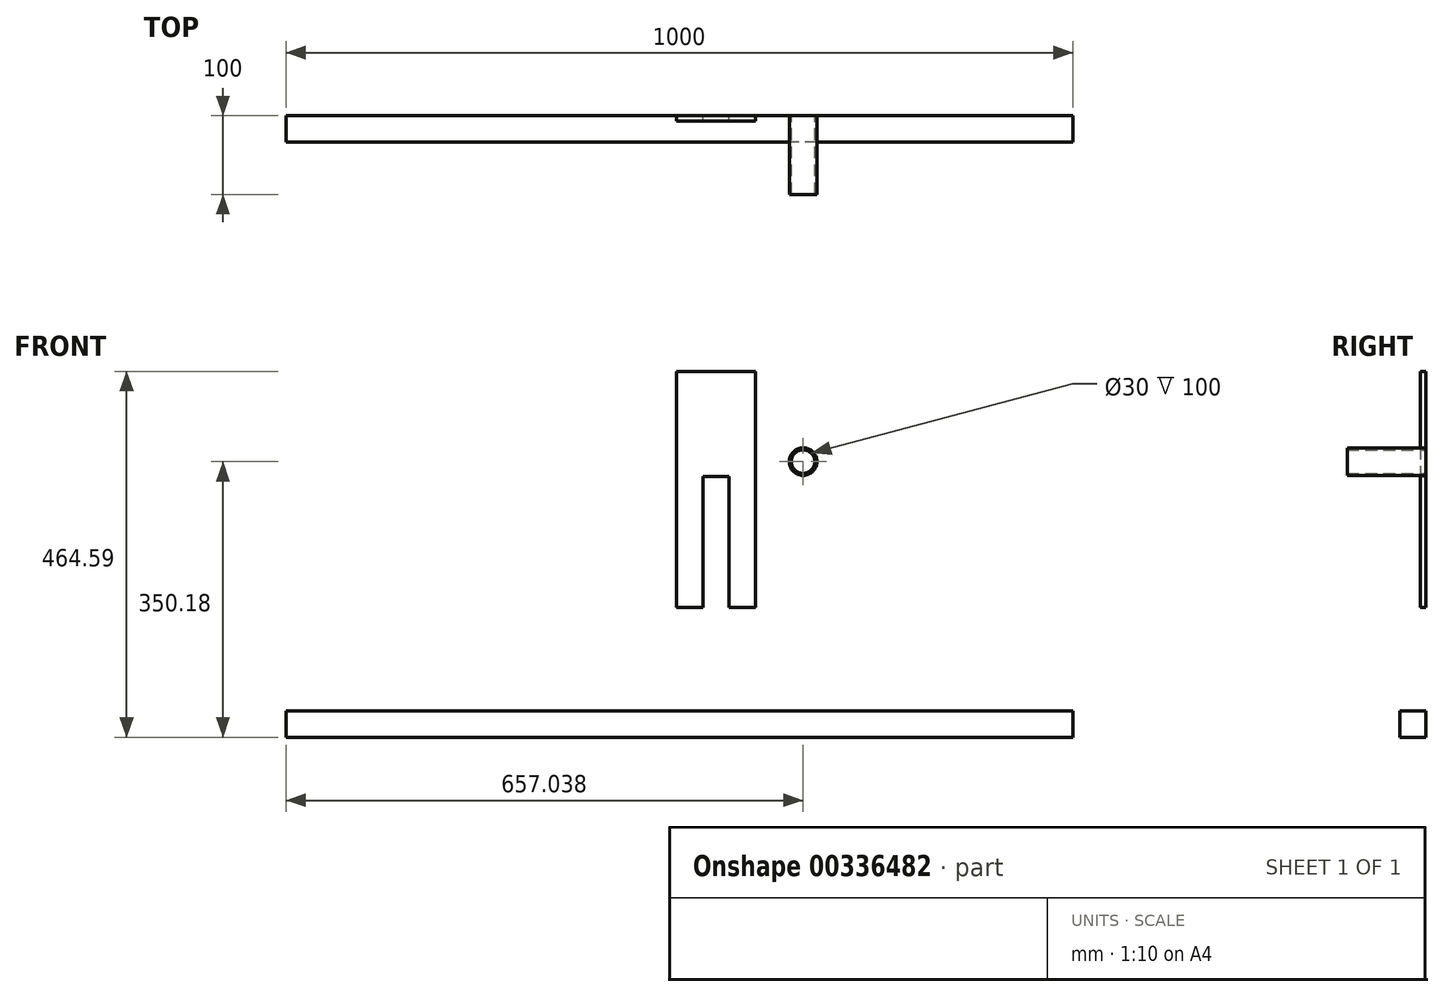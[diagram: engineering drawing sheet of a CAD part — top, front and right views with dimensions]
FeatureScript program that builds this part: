
annotation { "Feature Type Name" : "Feature", "Feature Type Description" : "" }
export const myFeature = defineFeature(function(context is Context, id is Id, definition is map)
    precondition{}
    {
        {
            var Q0;
            Q0=qCreatedBy(makeId("Front.planeOp"),FACE);
            var sketch = newSketch(context, id + "F0", { "sketchPlane" : qUnion([Q0])});
            skCircle(sketch, "E0", {"center": v(-34.7, 0) * mm, "radius": 15 * mm});
            skCircle(sketch, "E1", {"center": v(-34.7, 0) * mm, "radius": 17.5 * mm});
            skSolve(sketch);
        }
        {
            var Q0;
            Q0 = qSketchRegion(id + "F0", true);
            extrude(context, id + "F1", {"entities" : qUnion([Q0]), "depth" : 100 * mm});
        }
        {
            var Q0;
            Q0=qCreatedBy(makeId("Front.planeOp"),FACE);
            var sketch = newSketch(context, id + "F2", { "sketchPlane" : qUnion([Q0])});
            skLineSegment(sketch, "E2.bottom", {"start": v(-95.28, 114.41) * mm, "end": v(-195.28, 114.41) * mm});
            skLineSegment(sketch, "E2.top", {"start": v(-95.28, -185.59) * mm, "end": v(-128.58, -185.59) * mm});
            skLineSegment(sketch, "E2.left", {"start": v(-95.28, 114.41) * mm, "end": v(-95.28, -185.59) * mm});
            skLineSegment(sketch, "E2.right", {"start": v(-195.28, 114.41) * mm, "end": v(-195.28, -185.59) * mm});
            skPoint(sketch, "E3", {"position": v(-161.98, -185.59) * mm});
            skPoint(sketch, "E4", {"position": v(-128.58, -185.59) * mm});
            skLineSegment(sketch, "E5", {"start": v(-161.98, -185.59) * mm, "end": v(-161.98, -18.8) * mm});
            skLineSegment(sketch, "E6", {"start": v(-161.98, -18.8) * mm, "end": v(-128.58, -18.8) * mm});
            skLineSegment(sketch, "E7", {"start": v(-128.58, -18.8) * mm, "end": v(-128.58, -185.59) * mm});
            skLineSegment(sketch, "E8.trimOffspring", {"start": v(-161.98, -185.59) * mm, "end": v(-195.28, -185.59) * mm});
            skSolve(sketch);
        }
        {
            var Q0;
            Q0 = qSketchRegion(id + "F2", true);
            extrude(context, id + "F3", {"entities" : qUnion([Q0]), "depth" : 7 * mm});
        }
        {
            var Q0;
            Q0=qCreatedBy(makeId("Front.planeOp"),FACE);
            var sketch = newSketch(context, id + "F4", { "sketchPlane" : qUnion([Q0])});
            skLineSegment(sketch, "E9", {"start": v(-691.73, -316.88) * mm, "end": v(-691.73, -350.18) * mm});
            skLineSegment(sketch, "E10", {"start": v(-691.73, -350.18) * mm, "end": v(308.27, -350.18) * mm});
            skLineSegment(sketch, "E11", {"start": v(308.27, -350.18) * mm, "end": v(308.27, -316.88) * mm});
            skLineSegment(sketch, "E12", {"start": v(308.27, -316.88) * mm, "end": v(-691.73, -316.88) * mm});
            skSolve(sketch);
        }
        {
            var Q0;
            Q0=makeQuery(id+"F4.imprint","IMPRINT",FACE,{"disambiguationData":[TD([[makeQuery(id+"F4.imprint","IMPRINT",EDGE,{"derivedFrom":sQuery(id+"F4.wireOp",EDGE,"E9")}),1.0]])]});
            extrude(context, id + "F5", {"entities" : qUnion([Q0]), "depth" : 33.3 * mm});
        }
    });
